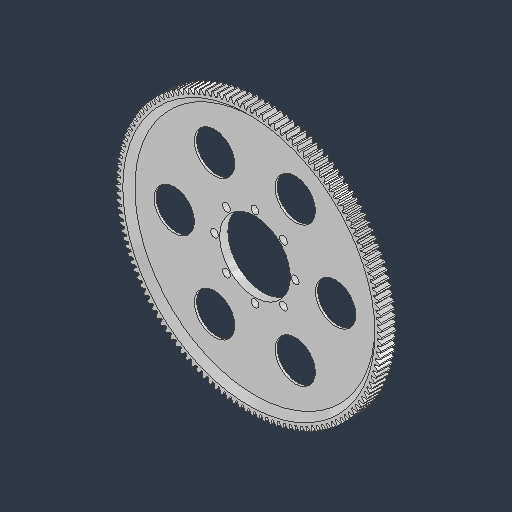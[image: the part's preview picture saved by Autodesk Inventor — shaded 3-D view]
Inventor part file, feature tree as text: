
AUTODESK INVENTOR PART (.ipt)
format: ipt  version: 2024.3 (Build 283343000, 343)  size: 1,058,304 bytes
history: native  units: mm (DEFAULTED — no unit token found)
features: sketch x6, other x4, extrude x3, plane x3, hole x3, pattern_circular x3, fillet x2, chamfer x1, mirror x1, delete_face x1, projected_geometry x1
ambient origin geometry x8: Origin, YZ Plane, XZ Plane, XY Plane, X Axis, Y Axis, Z Axis, Center Point
bodies: Solid1 (feature_tree)
feature tree (28):
  extrude  "Extrusion1"  Depth=9.017mm TaperAngle=0.0deg
  plane  "Work Plane1"
  plane  "Work Plane2"
  plane  "Work Plane3"
  other  "Spur Gear"
  hole  "Hole1"  [1 undecoded]
  extrude  "Extrusion2"  TaperAngle=0.0deg  [1 undecoded]
  chamfer  "Chamfer1"  Distance=101.219mm
  mirror  "Mirror1"
  hole  "Hole2"  [1 undecoded]
  pattern_circular  "Circular Pattern3"  [2 undecoded]
  delete_face  "Delete Face1"
  hole  "Hole3"  [1 undecoded]
  pattern_circular  "Circular Pattern4"  [2 undecoded]
  other  "WATERJET SKETCH"
  extrude  "Extrusion3"  Depth=3.81mm
  fillet  "Fillet1"  Radius=1.5875mm
  pattern_circular  "Circular Pattern2"  [2 undecoded]
  fillet  "Fillet2"  [1 undecoded]
  sketch  "Sketch1"  dims[d0=167.332752mm d1=9.017mm d2=0.0mm]
  other  "Srf1"
  sketch  "Sketch3"  dims[d3=168.75mm d4=76.2mm d5=0.0mm]
  sketch  "Sketch4"  dims[d6=0.0mm d7=0.232711mm d9=0.0mm d14=0.0mm d15=101.219mm]
  sketch  "Sketch5"  dims[d16=0.0mm d17=0.0mm d18=0.0mm d19=101.219mm]
  sketch  "Sketch6"  dims[d20=44.45mm d21=19.05mm d22=9.525mm d23=6.35mm d24=14.3117mm d25=25.4mm d26=20.594885mm]
  sketch  "Sketch7"  dims[d27=6.35mm d28=50.8mm d29=3.81mm d30=0.0mm d31=3.175mm d32=3.175mm d33=1.5875mm d34=1.5875mm d35=45.0deg d36=25.4mm d37=0.0mm d41=1.5875mm d42=0.762mm d43=80.0mm d44=360.0deg d46=0.762mm d47=3.81mm d48=3.175mm d49=45.0deg d50=25.4mm d51=19.05mm d52=9.525mm d53=6.35mm d54=14.3117mm d55=25.4mm d56=20.594885mm d57=50.8mm d58=60.0mm d59=360.0deg d61=25.4mm d62=4.9784mm d63=19.05mm d64=9.779mm d65=1.9558mm d66=14.3117mm d67=25.4mm d68=20.594885mm d69=80.0mm d70=360.0deg]
  other  "Pitch Diameter"
  projected_geometry  "Project Cut Edges1"
note: 11 required parameter values undecoded (feature->parameter linkage not recoverable at this tier; creation-order binding heuristic only, values carry confidence <= 0.55)
